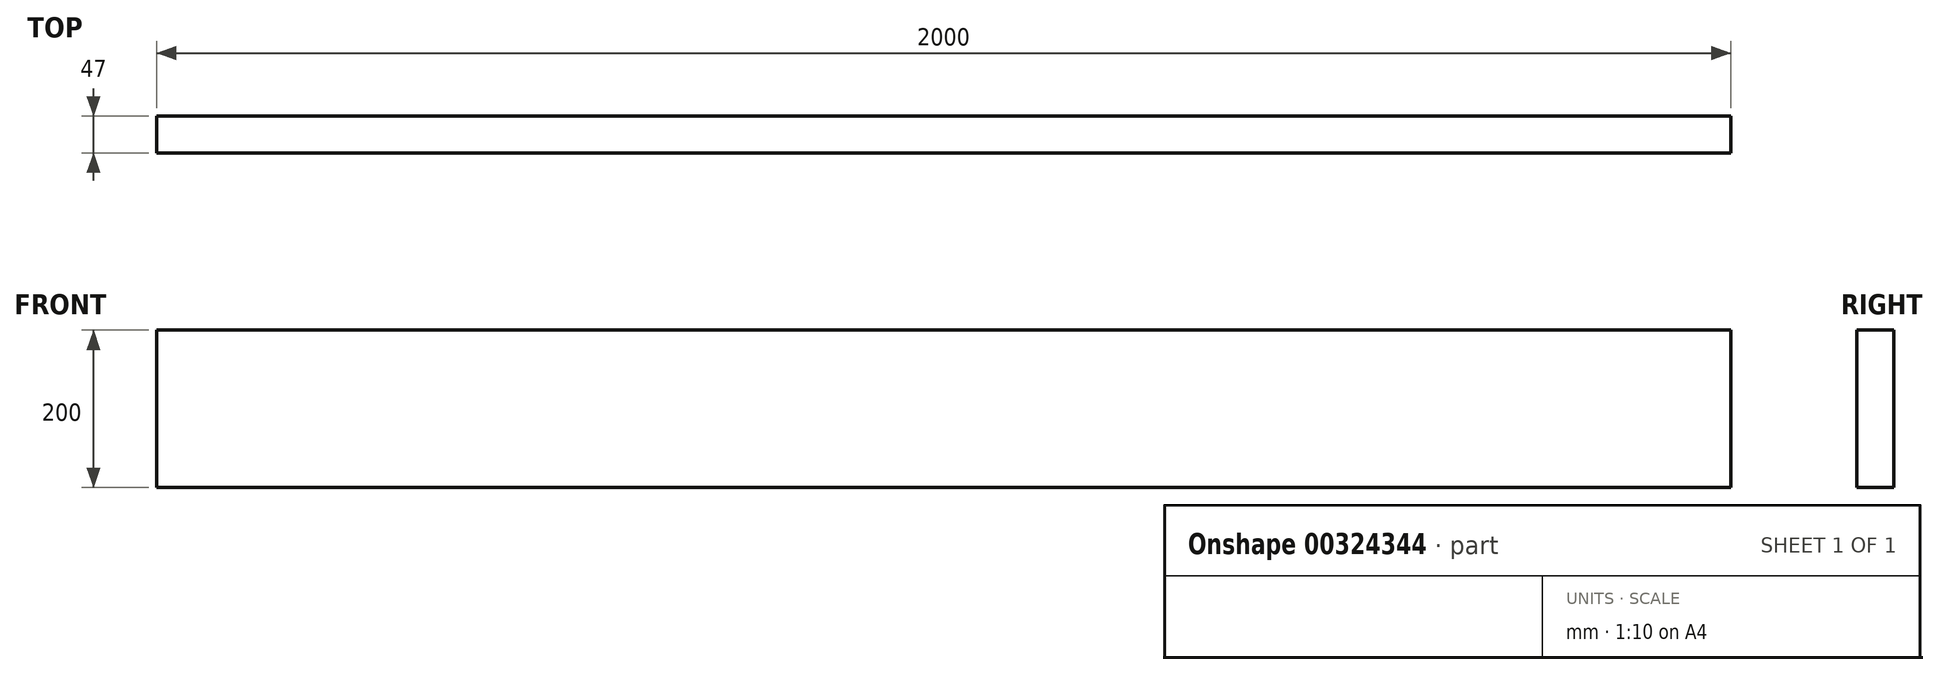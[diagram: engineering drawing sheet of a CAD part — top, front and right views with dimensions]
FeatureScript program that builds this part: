
annotation { "Feature Type Name" : "Feature", "Feature Type Description" : "" }
export const myFeature = defineFeature(function(context is Context, id is Id, definition is map)
    precondition{}
    {
        {
            var Q0;
            Q0=qCreatedBy(makeId("Top.planeOp"),FACE);
            var sketch = newSketch(context, id + "F0", { "sketchPlane" : qUnion([Q0])});
            skLineSegment(sketch, "E0.bottom", {"start": v(1000, -23.5) * mm, "end": v(-1000, -23.5) * mm});
            skLineSegment(sketch, "E0.top", {"start": v(1000, 23.5) * mm, "end": v(-1000, 23.5) * mm});
            skLineSegment(sketch, "E0.left", {"start": v(1000, -23.5) * mm, "end": v(1000, 23.5) * mm});
            skLineSegment(sketch, "E0.right", {"start": v(-1000, -23.5) * mm, "end": v(-1000, 23.5) * mm});
            skPoint(sketch, "E0.middle", {"position": v(0, 0) * mm});
            skSolve(sketch);
        }
        {
            var Q0;
            Q0=makeQuery(id+"F0.imprint","IMPRINT",FACE,{"disambiguationData":[TD([[makeQuery(id+"F0.imprint","IMPRINT",EDGE,{"derivedFrom":sQuery(id+"F0.wireOp",EDGE,"E0.bottom")}),-1.0]])]});
            extrude(context, id + "F1", {"entities" : qUnion([Q0]), "depth" : 200 * mm});
        }
    });
